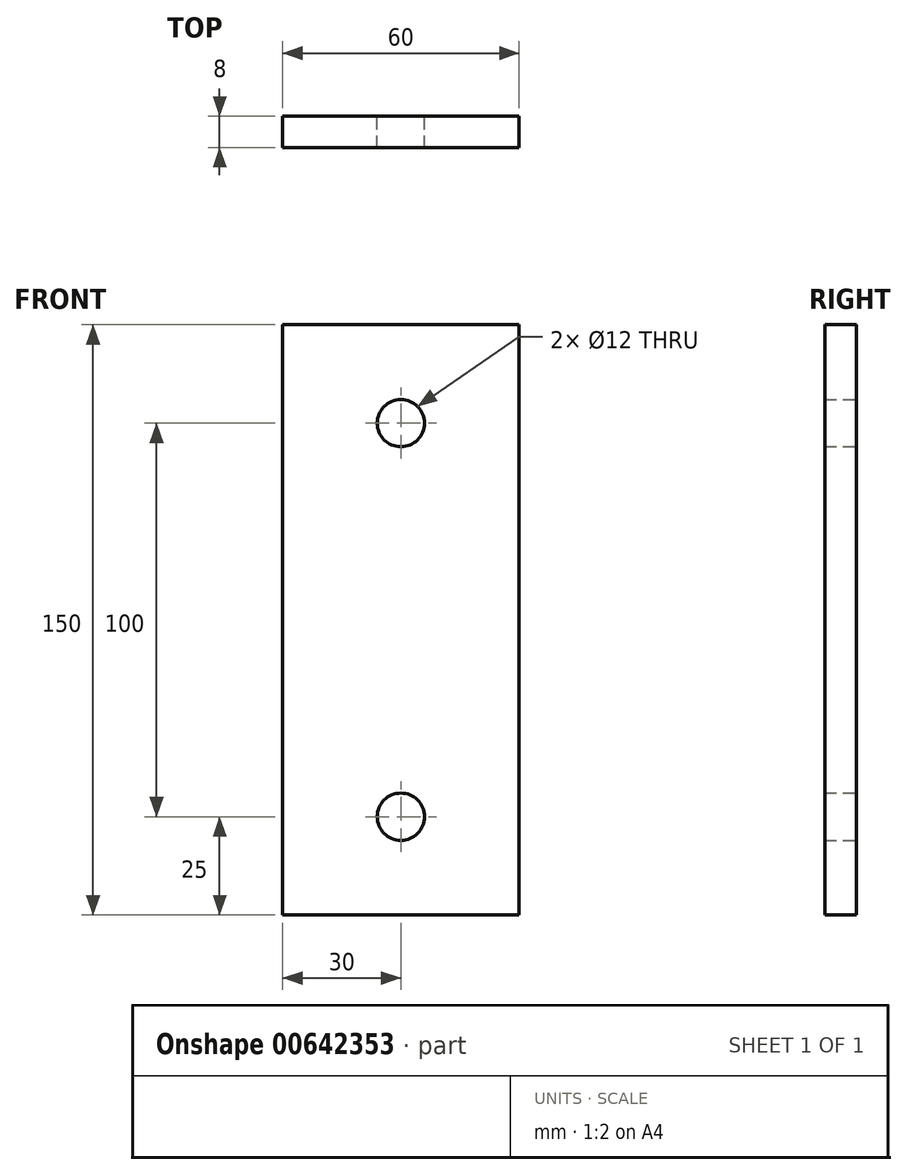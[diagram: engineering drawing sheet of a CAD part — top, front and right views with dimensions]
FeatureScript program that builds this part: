
annotation { "Feature Type Name" : "Feature", "Feature Type Description" : "" }
export const myFeature = defineFeature(function(context is Context, id is Id, definition is map)
    precondition{}
    {
        {
            var Q0;
            Q0=qCreatedBy(makeId("Front.planeOp"),FACE);
            var sketch = newSketch(context, id + "F0", { "sketchPlane" : qUnion([Q0])});
            skLineSegment(sketch, "E0.bottom", {"start": v(30, 75) * mm, "end": v(-30, 75) * mm});
            skLineSegment(sketch, "E0.top", {"start": v(30, -75) * mm, "end": v(-30, -75) * mm});
            skLineSegment(sketch, "E0.left", {"start": v(30, 75) * mm, "end": v(30, -75) * mm});
            skLineSegment(sketch, "E0.right", {"start": v(-30, 75) * mm, "end": v(-30, -75) * mm});
            skPoint(sketch, "E0.middle", {"position": v(0, 0) * mm});
            skCircle(sketch, "E1", {"center": v(0, 50) * mm, "radius": 6 * mm});
            skCircle(sketch, "E2", {"center": v(0, -50) * mm, "radius": 6 * mm});
            skSolve(sketch);
        }
        {
            var Q0;
            Q0=makeQuery(id+"F0.imprint","IMPRINT",FACE,{"disambiguationData":[TD([[makeQuery(id+"F0.imprint","IMPRINT",EDGE,{"derivedFrom":sQuery(id+"F0.wireOp",EDGE,"E0.bottom")}),1.0]])]});
            extrude(context, id + "F1", {"entities" : qUnion([Q0]), "endBound" : BoundingType.SYMMETRIC, "depth" : 8 * mm, "offsetDistance" : 25 * mm});
        }
    });
